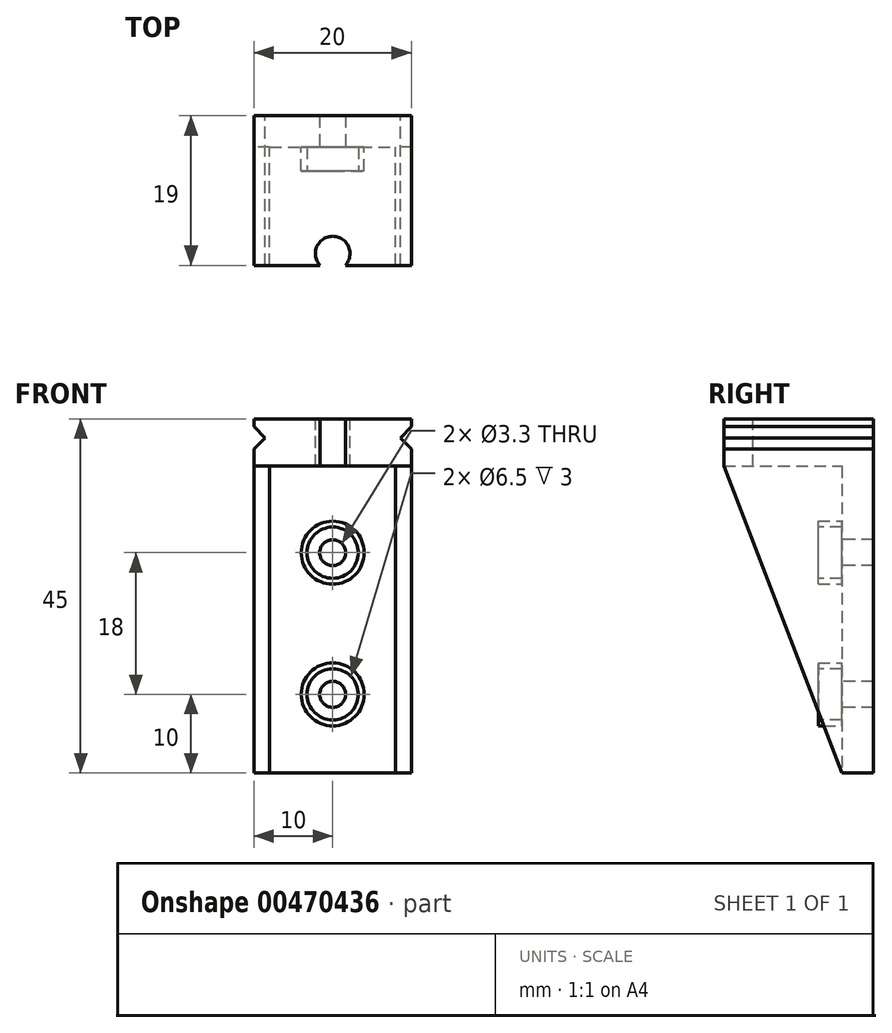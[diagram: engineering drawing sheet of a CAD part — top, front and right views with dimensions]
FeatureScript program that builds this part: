
annotation { "Feature Type Name" : "Feature", "Feature Type Description" : "" }
export const myFeature = defineFeature(function(context is Context, id is Id, definition is map)
    precondition{}
    {
        {
            var Q0;
            Q0=qCreatedBy(makeId("Front.planeOp"),FACE);
            var sketch = newSketch(context, id + "F0", { "sketchPlane" : qUnion([Q0])});
            skLineSegment(sketch, "E0.bottom", {"start": v(10, -22.5) * mm, "end": v(-10, -22.5) * mm});
            skLineSegment(sketch, "E0.top", {"start": v(10, 22.5) * mm, "end": v(-10, 22.5) * mm});
            skLineSegment(sketch, "E0.left", {"start": v(10, -22.5) * mm, "end": v(10, 22.5) * mm});
            skLineSegment(sketch, "E0.right", {"start": v(-10, -22.5) * mm, "end": v(-10, 22.5) * mm});
            skPoint(sketch, "E0.middle", {"position": v(0, 0) * mm});
            skLineSegment(sketch, "E1", {"start": v(10, 21.5) * mm, "end": v(8.59, 20.09) * mm});
            skLineSegment(sketch, "E2", {"start": v(8.59, 20.09) * mm, "end": v(10, 18.67) * mm});
            skLineSegment(sketch, "E3.MirrorCS", {"start": v(-10, 21.5) * mm, "end": v(-8.59, 20.09) * mm});
            skLineSegment(sketch, "E4.MirrorCS", {"start": v(-8.59, 20.09) * mm, "end": v(-10, 18.67) * mm});
            skSolve(sketch);
        }
        {
            var Q0;
            {var subQ3=sQuery(id+"F0.wireOp",EDGE,"E0.bottom");Q0=makeQuery(id+"F0.imprint","IMPRINT",FACE,{"disambiguationData":[TD([[makeQuery(id+"F0.imprint","IMPRINT",EDGE,{"derivedFrom":subQ3}),-1.0]])]});}
            extrude(context, id + "F1", {"entities" : qUnion([Q0]), "depth" : 4 * mm, "offsetDistance" : 25 * mm});
        }
        {
            var Q0;
            Q0=makeQuery(id+"F1.opExtrude","CAP_FACE",FACE,{"disambiguationData":[OSD([sQuery(id+"F0.wireOp",EDGE,"E0.bottom"),sQuery(id+"F0.wireOp",EDGE,"E0.top"),sQuery(id+"F0.wireOp",EDGE,"E0.left"),sQuery(id+"F0.wireOp",EDGE,"E0.right")])],"isStart":false});
            var sketch = newSketch(context, id + "F2", { "sketchPlane" : qUnion([Q0])});
            skLineSegment(sketch, "E5.top", {"start": v(-10, 16.5) * mm, "end": v(10, 16.5) * mm});
            skSolve(sketch);
        }
        {
            var Q0;
            Q0 = qSketchRegion(id + "F2", true);
            var Q1;
            {var subQ5=sQuery(id+"F2.wireOp",EDGE,"E5.top");Q1=makeQuery(id+"F2.imprint","IMPRINT",FACE,{"disambiguationData":[TD([[makeQuery(id+"F2.imprint","IMPRINT",EDGE,{"derivedFrom":subQ5}),1.0]])]});}
            extrude(context, id + "F3", {"entities" : qUnion([Q0, Q1]), "operationType" : NewBodyOperationType.ADD, "depth" : 15 * mm, "offsetDistance" : 25 * mm});
        }
        {
            var Q0;
            Q0=makeQuery(id+"F1.opExtrude","CAP_FACE",FACE,{"disambiguationData":[OSD([sQuery(id+"F0.wireOp",EDGE,"E0.bottom"),sQuery(id+"F0.wireOp",EDGE,"E0.top"),sQuery(id+"F0.wireOp",EDGE,"E0.left"),sQuery(id+"F0.wireOp",EDGE,"E0.right")])],"isStart":false});
            var sketch = newSketch(context, id + "F4", { "sketchPlane" : qUnion([Q0])});
            skLineSegment(sketch, "E6", {"start": v(0, -22.5) * mm, "end": v(0, 22.64) * mm, "construction": true});
            skLineSegment(sketch, "E7", {"start": v(10, 5.5) * mm, "end": v(-10, 5.5) * mm, "construction": true});
            skLineSegment(sketch, "E8", {"start": v(10, -12.5) * mm, "end": v(-10, -12.5) * mm, "construction": true});
            skCircle(sketch, "E9", {"center": v(0, 5.5) * mm, "radius": 4 * mm});
            skCircle(sketch, "E10", {"center": v(0, -12.5) * mm, "radius": 4 * mm});
            skSolve(sketch);
        }
        {
            var Q0;
            Q0 = qSketchRegion(id + "F4", true);
            extrude(context, id + "F5", {"entities" : qUnion([Q0]), "operationType" : NewBodyOperationType.ADD, "depth" : 3 * mm});
        }
        {
            var Q0;
            Q0=makeQuery(id+"F5.opExtrude","CAP_FACE",FACE,{"disambiguationData":[OSD([sQuery(id+"F4.wireOp",EDGE,"E10")])],"isStart":false});
            var sketch = newSketch(context, id + "F6", { "sketchPlane" : qUnion([Q0])});
            skPoint(sketch, "E11", {"position": v(0, 5.5) * mm});
            skPoint(sketch, "E12", {"position": v(0, -12.5) * mm});
            skSolve(sketch);
        }
        {
            var Q0;
            Q0=sQuery(id+"F6.wireOp",VERTEX,"E11");
            var Q1;
            Q1=sQuery(id+"F6.wireOp",VERTEX,"E12");
            var Q2;
            Q2=makeQuery(id+"F1.opExtrude","SWEPT_BODY",BODY,{"disambiguationData":[OSD([sQuery(id+"F0.wireOp",EDGE,"E0.bottom"),sQuery(id+"F0.wireOp",EDGE,"E0.top"),sQuery(id+"F0.wireOp",EDGE,"E0.left"),sQuery(id+"F0.wireOp",EDGE,"E0.right")])]});
            hole(context, id + "F7", {"style" : HoleStyle.C_BORE, "endStyle" : HoleEndStyle.THROUGH, "standardTappedOrClearance" : lookupTablePath({ "standard" : "ISO", "fit" : "Normal", "size" : "M3", "type" : "Clearance" }), "standardBlindInLast" : lookupTablePath({ "fit" : "Standard", "standard" : "ISO", "size" : "M3", "type" : "Clearance" }), "holeDiameter" : 3.3 * mm, "cBoreDiameter" : 6.5 * mm, "cBoreDepth" : 3 * mm, "tappedDepth" : 12 * mm, "tapClearance" : 3, "locations" : qUnion([Q0, Q1]), "scope" : qUnion([Q2])});
        }
        {
            var Q0;
            Q0=makeQuery(id+"F1.opExtrude","CAP_FACE",FACE,{"disambiguationData":[OSD([sQuery(id+"F0.wireOp",EDGE,"E0.bottom"),sQuery(id+"F0.wireOp",EDGE,"E0.top"),sQuery(id+"F0.wireOp",EDGE,"E0.left"),sQuery(id+"F0.wireOp",EDGE,"E0.right")])],"isStart":false});
            var sketch = newSketch(context, id + "F8", { "sketchPlane" : qUnion([Q0])});
            skLineSegment(sketch, "E13.bottom", {"start": v(-10, 16.5) * mm, "end": v(-8, 16.5) * mm});
            skLineSegment(sketch, "E13.top", {"start": v(-10, -22.5) * mm, "end": v(-8, -22.5) * mm});
            skLineSegment(sketch, "E13.left", {"start": v(-10, 16.5) * mm, "end": v(-10, -22.5) * mm});
            skLineSegment(sketch, "E13.right", {"start": v(-8, 16.5) * mm, "end": v(-8, -22.5) * mm});
            skLineSegment(sketch, "E14.bottom", {"start": v(10, 16.5) * mm, "end": v(8, 16.5) * mm});
            skLineSegment(sketch, "E14.top", {"start": v(10, -22.5) * mm, "end": v(8, -22.5) * mm});
            skLineSegment(sketch, "E14.left", {"start": v(10, 16.5) * mm, "end": v(10, -22.5) * mm});
            skLineSegment(sketch, "E14.right", {"start": v(8, 16.5) * mm, "end": v(8, -22.5) * mm});
            skSolve(sketch);
        }
        {
            var Q0;
            Q0=makeQuery(id+"F8.imprint","IMPRINT",FACE,{"disambiguationData":[TD([[makeQuery(id+"F8.imprint","IMPRINT",EDGE,{"derivedFrom":sQuery(id+"F8.wireOp",EDGE,"E13.bottom")}),-1.0]])]});
            var Q1;
            Q1=makeQuery(id+"F8.imprint","IMPRINT",FACE,{"disambiguationData":[TD([[makeQuery(id+"F8.imprint","IMPRINT",EDGE,{"derivedFrom":sQuery(id+"F8.wireOp",EDGE,"E14.bottom")}),-1.0]])]});
            var Q2;
            Q2=makeQuery(id+"F1.opExtrude","SWEPT_BODY",BODY,{"disambiguationData":[OSD([sQuery(id+"F0.wireOp",EDGE,"E0.bottom"),sQuery(id+"F0.wireOp",EDGE,"E0.top"),sQuery(id+"F0.wireOp",EDGE,"E0.left"),sQuery(id+"F0.wireOp",EDGE,"E0.right")])]});
            var Q3;
            Q3=makeQuery(id+"F3.opExtrude","CAP_VERTEX",VERTEX,{"disambiguationData":[OSD([sQuery(id+"F0.wireOp",EDGE,"E0.right"),sQuery(id+"F2.wireOp",EDGE,"E5.top"),sQuery(id+"F2.wireOp",EDGE,"E5.left")])],"isStart":false});
            extrude(context, id + "F9", {"entities" : qUnion([Q0, Q1]), "operationType" : NewBodyOperationType.ADD, "endBound" : BoundingType.UP_TO_VERTEX, "endBoundEntityBody" : qUnion([Q2]), "endBoundEntityVertex" : qUnion([Q3]), "depth" : 25 * mm});
        }
        {
            var Q0;
            Q0=makeQuery(id+"F9.opExtrude","CAP_EDGE",EDGE,{"disambiguationData":[OSD([sQuery(id+"F8.wireOp",EDGE,"E13.top")])],"isStart":false});
            var Q1;
            Q1=makeQuery(id+"F9.opExtrude","CAP_EDGE",EDGE,{"disambiguationData":[OSD([sQuery(id+"F8.wireOp",EDGE,"E14.top")])],"isStart":false});
            chamfer(context, id + "F10", {"entities" : qUnion([Q0, Q1]), "chamferType" : ChamferType.TWO_OFFSETS, "width1" : 15 * mm, "oppositeDirection" : false, "width2" : 39 * mm, "tangentPropagation" : true});
        }
        {
            var Q0;
            {var subQ0=sQuery(id+"F0.wireOp",EDGE,"E0.top");Q0=makeQuery(id+"F3.boolean.opBoolean","MERGE",FACE,{"derivedFrom":[makeQuery(id+"F1.opExtrude","SWEPT_FACE",FACE,{"disambiguationData":[OSD([subQ0])]}),makeQuery(id+"F3.opExtrude","SWEPT_FACE",FACE,{"disambiguationData":[OSD([subQ0])]})]});}
            var sketch = newSketch(context, id + "F11", { "sketchPlane" : qUnion([Q0])});
            skLineSegment(sketch, "E15", {"start": v(0, -19) * mm, "end": v(0, 0) * mm, "construction": true});
            skLineSegment(sketch, "E16", {"start": v(-10, -17.5) * mm, "end": v(10, -17.5) * mm, "construction": true});
            skPoint(sketch, "E17", {"position": v(0, -17.5) * mm});
            skSolve(sketch);
        }
        {
            var Q0;
            Q0=sQuery(id+"F11.wireOp",VERTEX,"E17");
            var Q1;
            Q1=makeQuery(id+"F1.opExtrude","SWEPT_BODY",BODY,{"disambiguationData":[OSD([sQuery(id+"F0.wireOp",EDGE,"E0.bottom"),sQuery(id+"F0.wireOp",EDGE,"E0.top"),sQuery(id+"F0.wireOp",EDGE,"E0.left"),sQuery(id+"F0.wireOp",EDGE,"E0.right"),sQuery(id+"F0.wireOp",EDGE,"E1"),sQuery(id+"F0.wireOp",EDGE,"E2"),sQuery(id+"F0.wireOp",EDGE,"E3.MirrorCS"),sQuery(id+"F0.wireOp",EDGE,"E4.MirrorCS")])]});
            hole(context, id + "F12", {"style" : HoleStyle.SIMPLE, "endStyle" : HoleEndStyle.THROUGH, "standardTappedOrClearance" : lookupTablePath({ "standard" : "ISO", "fit" : "Normal", "size" : "M4", "type" : "Clearance" }), "standardBlindInLast" : lookupTablePath({ "fit" : "Standard", "standard" : "ISO", "size" : "M4", "type" : "Clearance" }), "holeDiameter" : 4.4 * mm, "isTappedThrough" : true, "tappedDepth" : 12 * mm, "tapClearance" : 3, "locations" : qUnion([Q0]), "scope" : qUnion([Q1])});
        }
    });
